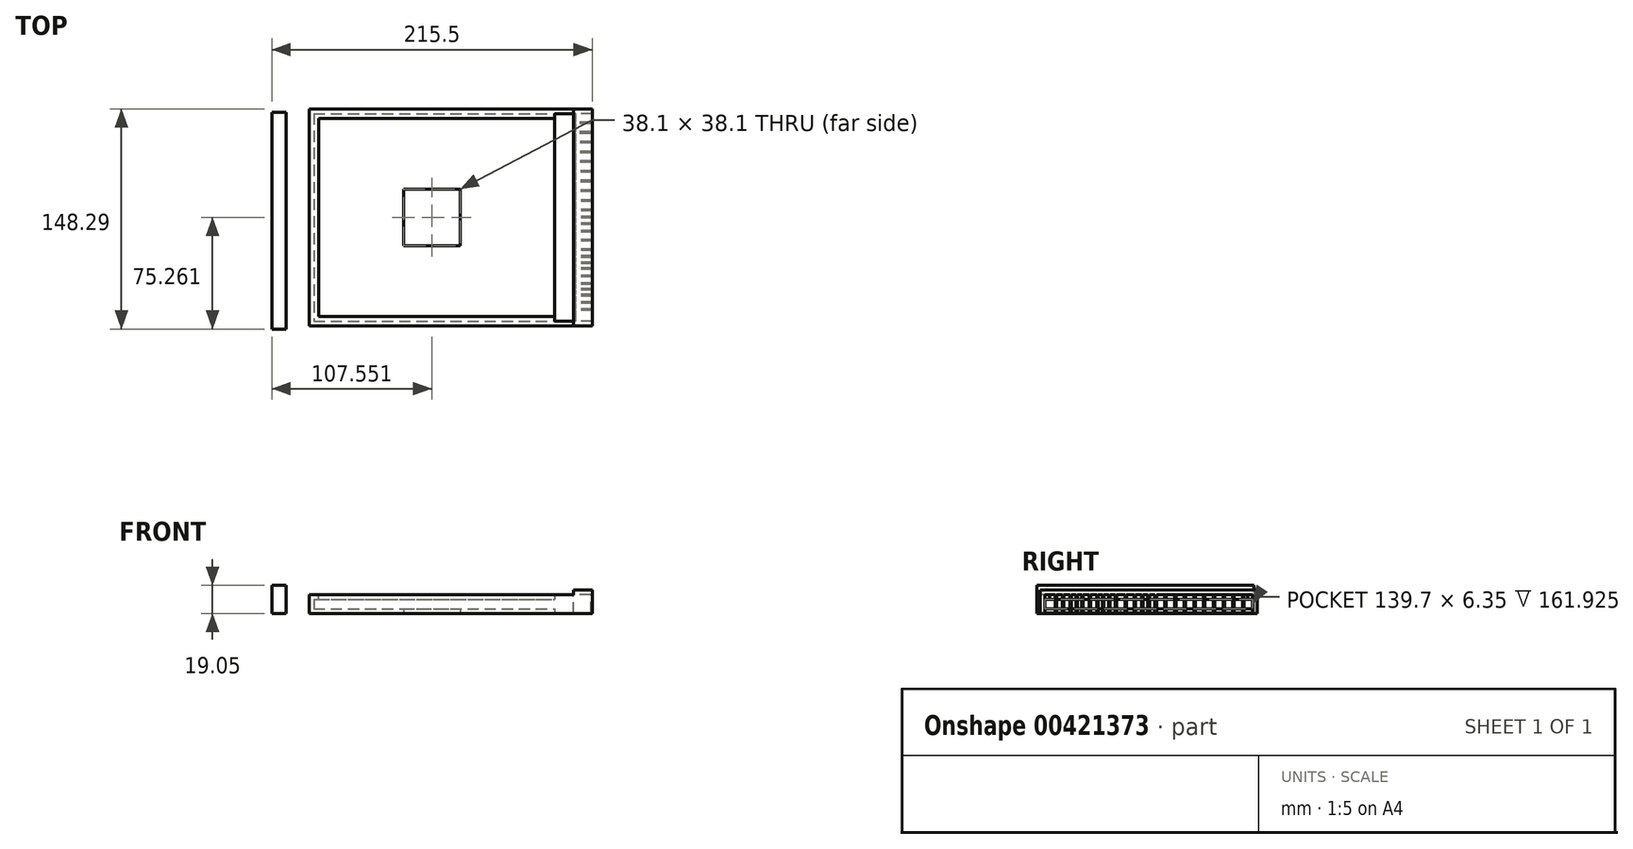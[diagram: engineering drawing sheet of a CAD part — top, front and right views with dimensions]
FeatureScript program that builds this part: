
annotation { "Feature Type Name" : "Feature", "Feature Type Description" : "" }
export const myFeature = defineFeature(function(context is Context, id is Id, definition is map)
    precondition{}
    {
        {
            var Q0;
            Q0=qCreatedBy(makeId("Top.planeOp"),FACE);
            var sketch = newSketch(context, id + "F0", { "sketchPlane" : qUnion([Q0])});
            skLineSegment(sketch, "E0.right", {"start": v(9.16, 77.9) * mm, "end": v(9.16, -42.76) * mm});
            skLineSegment(sketch, "E1.bottom", {"start": v(-155.94, 100.12) * mm, "end": v(9.16, 100.12) * mm});
            skLineSegment(sketch, "E1.top", {"start": v(-155.94, -45.93) * mm, "end": v(9.16, -45.93) * mm});
            skLineSegment(sketch, "E1.left", {"start": v(-155.94, 100.12) * mm, "end": v(-155.94, -45.93) * mm});
            skLineSegment(sketch, "E2", {"start": v(9.16, -42.76) * mm, "end": v(9.16, -45.93) * mm});
            skLineSegment(sketch, "E3", {"start": v(9.16, 77.9) * mm, "end": v(9.16, 100.12) * mm});
            skLineSegment(sketch, "E4.bottom", {"start": v(-92.44, 8.04) * mm, "end": v(-54.34, 8.04) * mm});
            skLineSegment(sketch, "E4.top", {"start": v(-92.44, 46.14) * mm, "end": v(-54.34, 46.14) * mm});
            skLineSegment(sketch, "E4.left", {"start": v(-92.44, 8.04) * mm, "end": v(-92.44, 46.14) * mm});
            skLineSegment(sketch, "E4.right", {"start": v(-54.34, 8.04) * mm, "end": v(-54.34, 46.14) * mm});
            skSolve(sketch);
        }
        {
            var Q0;
            Q0=makeQuery(id+"F0.imprint","IMPRINT",FACE,{"disambiguationData":[TD([[makeQuery(id+"F0.imprint","IMPRINT",EDGE,{"derivedFrom":sQuery(id+"F0.wireOp",EDGE,"E0.right")}),-1.0]])]});
            extrude(context, id + "F1", {"entities" : qUnion([Q0]), "depth" : 12.7 * mm});
        }
        {
            var Q0;
            Q0=makeQuery(id+"F1.opExtrude","SWEPT_FACE",FACE,{"disambiguationData":[OSD([sQuery(id+"F0.wireOp",EDGE,"E0.right"),sQuery(id+"F0.wireOp",EDGE,"E2"),sQuery(id+"F0.wireOp",EDGE,"E3")])]});
            var sketch = newSketch(context, id + "F2", { "sketchPlane" : qUnion([Q0])});
            skLineSegment(sketch, "E5.bottom", {"start": v(96.94, 9.52) * mm, "end": v(-42.76, 9.52) * mm});
            skLineSegment(sketch, "E5.top", {"start": v(96.94, 3.17) * mm, "end": v(-42.76, 3.17) * mm});
            skLineSegment(sketch, "E5.left", {"start": v(96.94, 9.52) * mm, "end": v(96.94, 3.17) * mm});
            skLineSegment(sketch, "E5.right", {"start": v(-42.76, 9.52) * mm, "end": v(-42.76, 3.17) * mm});
            skSolve(sketch);
        }
        {
            var Q0;
            Q0 = qSketchRegion(id + "F2", true);
            extrude(context, id + "F3", {"entities" : qUnion([Q0]), "operationType" : NewBodyOperationType.REMOVE, "oppositeDirection" : true, "depth" : 161.92 * mm});
        }
        {
            var Q0;
            Q0=makeQuery(id+"F1.opExtrude","CAP_FACE",FACE,{"disambiguationData":[OSD([sQuery(id+"F0.wireOp",EDGE,"E0.right"),sQuery(id+"F0.wireOp",EDGE,"E1.bottom"),sQuery(id+"F0.wireOp",EDGE,"E1.top"),sQuery(id+"F0.wireOp",EDGE,"E1.left"),sQuery(id+"F0.wireOp",EDGE,"E2"),sQuery(id+"F0.wireOp",EDGE,"E3")])],"isStart":false});
            var sketch = newSketch(context, id + "F4", { "sketchPlane" : qUnion([Q0])});
            skLineSegment(sketch, "E6.bottom", {"start": v(-149.59, 93.77) * mm, "end": v(9.16, 93.77) * mm});
            skLineSegment(sketch, "E6.top", {"start": v(-149.59, -39.58) * mm, "end": v(9.16, -39.58) * mm});
            skLineSegment(sketch, "E6.left", {"start": v(-149.59, 93.77) * mm, "end": v(-149.59, -39.58) * mm});
            skLineSegment(sketch, "E6.right", {"start": v(9.16, 93.77) * mm, "end": v(9.16, -39.58) * mm});
            skPoint(sketch, "E7.end.orphan", {"position": v(-149.59, 30.07) * mm});
            skPoint(sketch, "E7.start.orphan", {"position": v(-155.94, 30.07) * mm});
            skSolve(sketch);
        }
        {
            var Q0;
            Q0=makeQuery(id+"F4.imprint","IMPRINT",FACE,{"disambiguationData":[TD([[makeQuery(id+"F4.imprint","IMPRINT",EDGE,{"derivedFrom":sQuery(id+"F4.wireOp",EDGE,"E6.bottom")}),-1.0]])]});
            extrude(context, id + "F5", {"entities" : qUnion([Q0]), "operationType" : NewBodyOperationType.REMOVE, "oppositeDirection" : true, "depth" : 3.17 * mm});
        }
        {
            var Q0;
            Q0=makeQuery(id+"F1.opExtrude","SWEPT_FACE",FACE,{"disambiguationData":[OSD([sQuery(id+"F0.wireOp",EDGE,"E0.right"),sQuery(id+"F0.wireOp",EDGE,"E2"),sQuery(id+"F0.wireOp",EDGE,"E3")])]});
            var sketch = newSketch(context, id + "F6", { "sketchPlane" : qUnion([Q0])});
            skLineSegment(sketch, "E8", {"start": v(-42.76, 12.7) * mm, "end": v(-42.76, 0) * mm});
            skLineSegment(sketch, "E9", {"start": v(96.94, 12.7) * mm, "end": v(96.94, 0) * mm});
            skSolve(sketch);
        }
        {
            var Q0;
            {var subQ0=sQuery(id+"F0.wireOp",EDGE,"E2");var subQ1=sQuery(id+"F0.wireOp",EDGE,"E1.top");var subQ2=makeQuery(id+"F1.opExtrude","SWEPT_EDGE",EDGE,{"disambiguationData":[OSD([subQ1,subQ0])]});Q0=makeQuery(id+"F6.imprint","IMPRINT",FACE,{"disambiguationData":[TD([[makeQuery(id+"F6.imprint","IMPRINT",EDGE,{"derivedFrom":subQ2}),1.0]])]});}
            var Q1;
            {var subQ0=sQuery(id+"F0.wireOp",EDGE,"E3");var subQ1=sQuery(id+"F0.wireOp",EDGE,"E1.bottom");var subQ2=makeQuery(id+"F1.opExtrude","SWEPT_EDGE",EDGE,{"disambiguationData":[OSD([subQ1,subQ0])]});Q1=makeQuery(id+"F6.imprint","IMPRINT",FACE,{"disambiguationData":[TD([[makeQuery(id+"F6.imprint","IMPRINT",EDGE,{"derivedFrom":subQ2}),-1.0]])]});}
            extrude(context, id + "F7", {"entities" : qUnion([Q0, Q1]), "operationType" : NewBodyOperationType.ADD, "depth" : 25.4 * mm});
        }
        {
            var Q0;
            {var subQ0=sQuery(id+"F0.wireOp",EDGE,"E3");var subQ1=sQuery(id+"F0.wireOp",EDGE,"E2");var subQ2=sQuery(id+"F0.wireOp",EDGE,"E0.right");var subQ3=makeQuery(id+"F1.opExtrude","CAP_EDGE",EDGE,{"disambiguationData":[OSD([subQ2,subQ1,subQ0])],"isStart":true});var subQ4=sQuery(id+"F0.wireOp",EDGE,"E1.top");var subQ5=sQuery(id+"F0.wireOp",EDGE,"E1.bottom");Q0=makeQuery(id+"F7.boolean.opBoolean","MERGE",FACE,{"derivedFrom":[makeQuery(id+"F1.opExtrude","CAP_FACE",FACE,{"disambiguationData":[OSD([subQ2,subQ5,subQ4,sQuery(id+"F0.wireOp",EDGE,"E1.left"),subQ1,subQ0])],"isStart":true}),makeQuery(id+"F7.opExtrude","SWEPT_FACE",FACE,{"disambiguationData":[OSD([subQ2,subQ1,subQ0]),TDD([makeQuery(id+"F6.imprint","IMPRINT",EDGE,{"disambiguationData":[TD([[makeQuery(id+"F6.imprint","INTERSECT",VERTEX,{"derivedFrom":[subQ3,sQuery(id+"F6.wireOp",EDGE,"E9")]}),1.0]])],"derivedFrom":subQ3})])]}),makeQuery(id+"F7.opExtrude","SWEPT_FACE",FACE,{"disambiguationData":[OSD([subQ2,subQ1,subQ0]),TDD([makeQuery(id+"F6.imprint","IMPRINT",EDGE,{"disambiguationData":[TD([[makeQuery(id+"F6.imprint","INTERSECT",VERTEX,{"derivedFrom":[subQ3,sQuery(id+"F6.wireOp",EDGE,"E8")]}),-1.0]])],"derivedFrom":subQ3})])]})]});}
            var sketch = newSketch(context, id + "F8", { "sketchPlane" : qUnion([Q0])});
            skPoint(sketch, "E10.0", {"position": v(-180.94, 48.17) * mm});
            skLineSegment(sketch, "E11.0", {"start": v(-155.94, -100.12) * mm, "end": v(34.56, -100.12) * mm});
            skLineSegment(sketch, "E12.bottom", {"start": v(-180.94, 48.17) * mm, "end": v(-171.41, 48.17) * mm});
            skLineSegment(sketch, "E12.left", {"start": v(-180.94, 48.17) * mm, "end": v(-180.94, -97.88) * mm});
            skLineSegment(sketch, "E12.right", {"start": v(-171.41, 48.17) * mm, "end": v(-171.41, -97.88) * mm});
            skLineSegment(sketch, "E13", {"start": v(-171.41, -97.88) * mm, "end": v(-180.94, -97.88) * mm});
            skSolve(sketch);
        }
        {
            var Q0;
            Q0=makeQuery(id+"F8.imprint","IMPRINT",FACE,{"disambiguationData":[TD([[makeQuery(id+"F8.imprint","IMPRINT",EDGE,{"derivedFrom":sQuery(id+"F8.wireOp",EDGE,"E12.bottom")}),-1.0]])]});
            extrude(context, id + "F9", {"entities" : qUnion([Q0]), "oppositeDirection" : true, "depth" : 19.05 * mm});
        }
        {
            var Q0;
            {var subQ0=sQuery(id+"F0.wireOp",EDGE,"E1.top");Q0=makeQuery(id+"F9.boolean.opBoolean","MERGE",FACE,{"derivedFrom":[makeQuery(id+"F7.boolean.opBoolean","MERGE",FACE,{"derivedFrom":[makeQuery(id+"F1.opExtrude","SWEPT_FACE",FACE,{"disambiguationData":[OSD([subQ0])]}),makeQuery(id+"F7.opExtrude","SWEPT_FACE",FACE,{"disambiguationData":[OSD([subQ0,sQuery(id+"F0.wireOp",EDGE,"E2")])]})]}),makeQuery(id+"F9.opExtrude","SWEPT_FACE",FACE,{"disambiguationData":[OSD([sQuery(id+"F8.wireOp",EDGE,"E12.bottom")])]})]});}
            var sketch = newSketch(context, id + "F10", { "sketchPlane" : qUnion([Q0])});
            skLineSegment(sketch, "E14.bottom", {"start": v(34.56, 12.7) * mm, "end": v(21.86, 12.7) * mm});
            skLineSegment(sketch, "E14.top", {"start": v(34.56, 15.88) * mm, "end": v(21.86, 15.88) * mm});
            skLineSegment(sketch, "E14.left", {"start": v(34.56, 12.7) * mm, "end": v(34.56, 15.88) * mm});
            skLineSegment(sketch, "E14.right", {"start": v(21.86, 12.7) * mm, "end": v(21.86, 15.88) * mm});
            skSolve(sketch);
        }
        {
            var Q0;
            Q0=makeQuery(id+"F10.imprint","IMPRINT",FACE,{"disambiguationData":[TD([[makeQuery(id+"F10.imprint","IMPRINT",EDGE,{"derivedFrom":sQuery(id+"F10.wireOp",EDGE,"E14.bottom")}),1.0]])]});
            extrude(context, id + "F11", {"entities" : qUnion([Q0]), "operationType" : NewBodyOperationType.ADD, "oppositeDirection" : true, "depth" : 146.05 * mm});
        }
        {
            var Q0;
            Q0=makeQuery(id+"F11.opExtrude","SWEPT_FACE",FACE,{"disambiguationData":[OSD([sQuery(id+"F10.wireOp",EDGE,"E14.bottom")])]});
            var sketch = newSketch(context, id + "F12", { "sketchPlane" : qUnion([Q0])});
            skLineSegment(sketch, "E15.bottom", {"start": v(34.56, 35.67) * mm, "end": v(21.86, 35.67) * mm});
            skLineSegment(sketch, "E15.top", {"start": v(34.56, 34.67) * mm, "end": v(21.86, 34.67) * mm});
            skLineSegment(sketch, "E15.left", {"start": v(34.56, 35.67) * mm, "end": v(34.56, 34.67) * mm});
            skLineSegment(sketch, "E15.right", {"start": v(21.86, 35.67) * mm, "end": v(21.86, 34.67) * mm});
            skLineSegment(sketch, "E16.bottom", {"start": v(34.56, 25.88) * mm, "end": v(21.86, 25.88) * mm});
            skLineSegment(sketch, "E16.top", {"start": v(34.56, 24.88) * mm, "end": v(21.86, 24.88) * mm});
            skLineSegment(sketch, "E16.left", {"start": v(34.56, 25.88) * mm, "end": v(34.56, 24.88) * mm});
            skLineSegment(sketch, "E16.right", {"start": v(21.86, 25.88) * mm, "end": v(21.86, 24.88) * mm});
            skLineSegment(sketch, "E17.bottom", {"start": v(34.56, 21.93) * mm, "end": v(21.86, 21.93) * mm});
            skLineSegment(sketch, "E17.top", {"start": v(34.56, 20.93) * mm, "end": v(21.86, 20.93) * mm});
            skLineSegment(sketch, "E17.left", {"start": v(34.56, 21.93) * mm, "end": v(34.56, 20.93) * mm});
            skLineSegment(sketch, "E17.right", {"start": v(21.86, 21.93) * mm, "end": v(21.86, 20.93) * mm});
            skLineSegment(sketch, "E18.bottom", {"start": v(34.56, 18) * mm, "end": v(21.86, 18) * mm});
            skLineSegment(sketch, "E18.top", {"start": v(34.56, 17) * mm, "end": v(21.86, 17) * mm});
            skLineSegment(sketch, "E18.left", {"start": v(34.56, 18) * mm, "end": v(34.56, 17) * mm});
            skLineSegment(sketch, "E18.right", {"start": v(21.86, 18) * mm, "end": v(21.86, 17) * mm});
            skLineSegment(sketch, "E19.bottom", {"start": v(34.56, 30.9) * mm, "end": v(21.86, 30.9) * mm});
            skLineSegment(sketch, "E19.top", {"start": v(34.56, 29.9) * mm, "end": v(21.86, 29.9) * mm});
            skLineSegment(sketch, "E19.left", {"start": v(34.56, 30.9) * mm, "end": v(34.56, 29.9) * mm});
            skLineSegment(sketch, "E19.right", {"start": v(21.86, 30.9) * mm, "end": v(21.86, 29.9) * mm});
            skLineSegment(sketch, "E20.bottom", {"start": v(34.56, 12.93) * mm, "end": v(21.86, 12.93) * mm});
            skLineSegment(sketch, "E20.top", {"start": v(34.56, 11.93) * mm, "end": v(21.86, 11.93) * mm});
            skLineSegment(sketch, "E20.left", {"start": v(34.56, 12.93) * mm, "end": v(34.56, 11.93) * mm});
            skLineSegment(sketch, "E20.right", {"start": v(21.86, 12.93) * mm, "end": v(21.86, 11.93) * mm});
            skLineSegment(sketch, "E21.bottom", {"start": v(34.56, 7.84) * mm, "end": v(21.86, 7.84) * mm});
            skLineSegment(sketch, "E21.top", {"start": v(34.56, 6.84) * mm, "end": v(21.86, 6.84) * mm});
            skLineSegment(sketch, "E21.left", {"start": v(34.56, 7.84) * mm, "end": v(34.56, 6.84) * mm});
            skLineSegment(sketch, "E21.right", {"start": v(21.86, 7.84) * mm, "end": v(21.86, 6.84) * mm});
            skLineSegment(sketch, "E22.bottom", {"start": v(34.56, 4) * mm, "end": v(21.86, 4) * mm});
            skLineSegment(sketch, "E22.top", {"start": v(34.56, 3) * mm, "end": v(21.86, 3) * mm});
            skLineSegment(sketch, "E22.left", {"start": v(34.56, 4) * mm, "end": v(34.56, 3) * mm});
            skLineSegment(sketch, "E22.right", {"start": v(21.86, 4) * mm, "end": v(21.86, 3) * mm});
            skLineSegment(sketch, "E23.bottom", {"start": v(34.56, -0.16) * mm, "end": v(21.86, -0.16) * mm});
            skLineSegment(sketch, "E23.top", {"start": v(34.56, -1.16) * mm, "end": v(21.86, -1.16) * mm});
            skLineSegment(sketch, "E23.left", {"start": v(34.56, -0.16) * mm, "end": v(34.56, -1.16) * mm});
            skLineSegment(sketch, "E23.right", {"start": v(21.86, -0.16) * mm, "end": v(21.86, -1.16) * mm});
            skLineSegment(sketch, "E24.bottom", {"start": v(34.56, -4.65) * mm, "end": v(21.86, -4.65) * mm});
            skLineSegment(sketch, "E24.top", {"start": v(34.56, -5.65) * mm, "end": v(21.86, -5.65) * mm});
            skLineSegment(sketch, "E24.left", {"start": v(34.56, -4.65) * mm, "end": v(34.56, -5.65) * mm});
            skLineSegment(sketch, "E24.right", {"start": v(21.86, -4.65) * mm, "end": v(21.86, -5.65) * mm});
            skLineSegment(sketch, "E25.bottom", {"start": v(34.56, -11.24) * mm, "end": v(21.86, -11.24) * mm});
            skLineSegment(sketch, "E25.top", {"start": v(34.56, -12.24) * mm, "end": v(21.86, -12.24) * mm});
            skLineSegment(sketch, "E25.left", {"start": v(34.56, -11.24) * mm, "end": v(34.56, -12.24) * mm});
            skLineSegment(sketch, "E25.right", {"start": v(21.86, -11.24) * mm, "end": v(21.86, -12.24) * mm});
            skLineSegment(sketch, "E26.bottom", {"start": v(34.56, -17.2) * mm, "end": v(21.86, -17.2) * mm});
            skLineSegment(sketch, "E26.top", {"start": v(34.56, -18.2) * mm, "end": v(21.86, -18.2) * mm});
            skLineSegment(sketch, "E26.left", {"start": v(34.56, -17.2) * mm, "end": v(34.56, -18.2) * mm});
            skLineSegment(sketch, "E26.right", {"start": v(21.86, -17.2) * mm, "end": v(21.86, -18.2) * mm});
            skLineSegment(sketch, "E27.bottom", {"start": v(34.56, -22.35) * mm, "end": v(21.86, -22.35) * mm});
            skLineSegment(sketch, "E27.top", {"start": v(34.56, -23.35) * mm, "end": v(21.86, -23.35) * mm});
            skLineSegment(sketch, "E27.left", {"start": v(34.56, -22.35) * mm, "end": v(34.56, -23.35) * mm});
            skLineSegment(sketch, "E27.right", {"start": v(21.86, -22.35) * mm, "end": v(21.86, -23.35) * mm});
            skLineSegment(sketch, "E28.bottom", {"start": v(34.6, -26.6) * mm, "end": v(21.9, -26.6) * mm});
            skLineSegment(sketch, "E28.top", {"start": v(34.6, -27.6) * mm, "end": v(21.9, -27.6) * mm});
            skLineSegment(sketch, "E28.left", {"start": v(34.6, -26.6) * mm, "end": v(34.6, -27.6) * mm});
            skLineSegment(sketch, "E28.right", {"start": v(21.9, -26.6) * mm, "end": v(21.9, -27.6) * mm});
            skLineSegment(sketch, "E29.bottom", {"start": v(34.6, -31.37) * mm, "end": v(21.9, -31.37) * mm});
            skLineSegment(sketch, "E29.top", {"start": v(34.6, -32.37) * mm, "end": v(21.9, -32.37) * mm});
            skLineSegment(sketch, "E29.left", {"start": v(34.6, -31.37) * mm, "end": v(34.6, -32.37) * mm});
            skLineSegment(sketch, "E29.right", {"start": v(21.9, -31.37) * mm, "end": v(21.9, -32.37) * mm});
            skLineSegment(sketch, "E30.0.1.0", {"start": v(34.5, -37.9) * mm, "end": v(21.8, -37.9) * mm});
            skLineSegment(sketch, "E30.0.1.1", {"start": v(34.5, -38.9) * mm, "end": v(21.8, -38.9) * mm});
            skLineSegment(sketch, "E30.0.1.2", {"start": v(21.8, -37.9) * mm, "end": v(21.8, -38.9) * mm});
            skLineSegment(sketch, "E30.0.1.3", {"start": v(34.5, -37.9) * mm, "end": v(34.5, -38.9) * mm});
            skLineSegment(sketch, "E30.0.2.0", {"start": v(34.4, -44.43) * mm, "end": v(21.7, -44.43) * mm});
            skLineSegment(sketch, "E30.0.2.1", {"start": v(34.4, -45.43) * mm, "end": v(21.7, -45.43) * mm});
            skLineSegment(sketch, "E30.0.2.2", {"start": v(21.7, -44.43) * mm, "end": v(21.7, -45.43) * mm});
            skLineSegment(sketch, "E30.0.2.3", {"start": v(34.4, -44.43) * mm, "end": v(34.4, -45.43) * mm});
            skLineSegment(sketch, "E30.0.3.0", {"start": v(34.28, -50.97) * mm, "end": v(21.58, -50.97) * mm});
            skLineSegment(sketch, "E30.0.3.1", {"start": v(34.28, -51.97) * mm, "end": v(21.58, -51.97) * mm});
            skLineSegment(sketch, "E30.0.3.2", {"start": v(21.58, -50.97) * mm, "end": v(21.58, -51.97) * mm});
            skLineSegment(sketch, "E30.0.3.3", {"start": v(34.28, -50.97) * mm, "end": v(34.28, -51.97) * mm});
            skLineSegment(sketch, "E30.0.4.0", {"start": v(34.18, -57.5) * mm, "end": v(21.48, -57.5) * mm});
            skLineSegment(sketch, "E30.0.4.1", {"start": v(34.18, -58.5) * mm, "end": v(21.48, -58.5) * mm});
            skLineSegment(sketch, "E30.0.4.2", {"start": v(21.48, -57.5) * mm, "end": v(21.48, -58.5) * mm});
            skLineSegment(sketch, "E30.0.4.3", {"start": v(34.18, -57.5) * mm, "end": v(34.18, -58.5) * mm});
            skLineSegment(sketch, "E30.0.5.0", {"start": v(34.07, -64.04) * mm, "end": v(21.37, -64.04) * mm});
            skLineSegment(sketch, "E30.0.5.1", {"start": v(34.07, -65.04) * mm, "end": v(21.37, -65.04) * mm});
            skLineSegment(sketch, "E30.0.5.2", {"start": v(21.37, -64.04) * mm, "end": v(21.37, -65.04) * mm});
            skLineSegment(sketch, "E30.0.5.3", {"start": v(34.07, -64.04) * mm, "end": v(34.07, -65.04) * mm});
            skLineSegment(sketch, "E30.0.6.0", {"start": v(33.96, -70.57) * mm, "end": v(21.26, -70.57) * mm});
            skLineSegment(sketch, "E30.0.6.1", {"start": v(33.96, -71.57) * mm, "end": v(21.26, -71.57) * mm});
            skLineSegment(sketch, "E30.0.6.2", {"start": v(21.26, -70.57) * mm, "end": v(21.26, -71.57) * mm});
            skLineSegment(sketch, "E30.0.6.3", {"start": v(33.96, -70.57) * mm, "end": v(33.96, -71.57) * mm});
            skLineSegment(sketch, "E30.0.7.0", {"start": v(33.85, -77.1) * mm, "end": v(21.15, -77.1) * mm});
            skLineSegment(sketch, "E30.0.7.1", {"start": v(33.85, -78.1) * mm, "end": v(21.15, -78.1) * mm});
            skLineSegment(sketch, "E30.0.7.2", {"start": v(21.15, -77.1) * mm, "end": v(21.15, -78.1) * mm});
            skLineSegment(sketch, "E30.0.7.3", {"start": v(33.85, -77.1) * mm, "end": v(33.85, -78.1) * mm});
            skLineSegment(sketch, "E30.0.8.0", {"start": v(33.75, -83.64) * mm, "end": v(21.05, -83.64) * mm});
            skLineSegment(sketch, "E30.0.8.1", {"start": v(33.75, -84.64) * mm, "end": v(21.05, -84.64) * mm});
            skLineSegment(sketch, "E30.0.8.2", {"start": v(21.05, -83.64) * mm, "end": v(21.05, -84.64) * mm});
            skLineSegment(sketch, "E30.0.8.3", {"start": v(33.75, -83.64) * mm, "end": v(33.75, -84.64) * mm});
            skLineSegment(sketch, "E30.0.9.0", {"start": v(33.64, -90.17) * mm, "end": v(20.94, -90.17) * mm});
            skLineSegment(sketch, "E30.0.9.1", {"start": v(33.64, -91.17) * mm, "end": v(20.94, -91.17) * mm});
            skLineSegment(sketch, "E30.0.9.2", {"start": v(20.94, -90.17) * mm, "end": v(20.94, -91.17) * mm});
            skLineSegment(sketch, "E30.0.9.3", {"start": v(33.64, -90.17) * mm, "end": v(33.64, -91.17) * mm});
            skLineSegment(sketch, "E30.direction1", {"start": v(21.9, -32.37) * mm, "end": v(46.9, -32.37) * mm, "construction": true});
            skLineSegment(sketch, "E30.direction2", {"start": v(21.9, -32.37) * mm, "end": v(21.8, -38.9) * mm, "construction": true});
            skSolve(sketch);
        }
        {
            var Q0;
            Q0=makeQuery(id+"F12.imprint","IMPRINT",FACE,{"disambiguationData":[TD([[makeQuery(id+"F12.imprint","IMPRINT",EDGE,{"derivedFrom":sQuery(id+"F12.wireOp",EDGE,"E15.bottom")}),1.0]])]});
            var Q1;
            Q1=makeQuery(id+"F12.imprint","IMPRINT",FACE,{"disambiguationData":[TD([[makeQuery(id+"F12.imprint","IMPRINT",EDGE,{"derivedFrom":sQuery(id+"F12.wireOp",EDGE,"E19.bottom")}),1.0]])]});
            var Q2;
            Q2=makeQuery(id+"F12.imprint","IMPRINT",FACE,{"disambiguationData":[TD([[makeQuery(id+"F12.imprint","IMPRINT",EDGE,{"derivedFrom":sQuery(id+"F12.wireOp",EDGE,"E16.bottom")}),1.0]])]});
            var Q3;
            Q3=makeQuery(id+"F12.imprint","IMPRINT",FACE,{"disambiguationData":[TD([[makeQuery(id+"F12.imprint","IMPRINT",EDGE,{"derivedFrom":sQuery(id+"F12.wireOp",EDGE,"E17.bottom")}),1.0]])]});
            var Q4;
            Q4=makeQuery(id+"F12.imprint","IMPRINT",FACE,{"disambiguationData":[TD([[makeQuery(id+"F12.imprint","IMPRINT",EDGE,{"derivedFrom":sQuery(id+"F12.wireOp",EDGE,"E18.bottom")}),1.0]])]});
            var Q5;
            Q5=makeQuery(id+"F12.imprint","IMPRINT",FACE,{"disambiguationData":[TD([[makeQuery(id+"F12.imprint","IMPRINT",EDGE,{"derivedFrom":sQuery(id+"F12.wireOp",EDGE,"E20.bottom")}),1.0]])]});
            var Q6;
            Q6=makeQuery(id+"F12.imprint","IMPRINT",FACE,{"disambiguationData":[TD([[makeQuery(id+"F12.imprint","IMPRINT",EDGE,{"derivedFrom":sQuery(id+"F12.wireOp",EDGE,"E21.bottom")}),1.0]])]});
            var Q7;
            Q7=makeQuery(id+"F12.imprint","IMPRINT",FACE,{"disambiguationData":[TD([[makeQuery(id+"F12.imprint","IMPRINT",EDGE,{"derivedFrom":sQuery(id+"F12.wireOp",EDGE,"E22.bottom")}),1.0]])]});
            var Q8;
            Q8=makeQuery(id+"F12.imprint","IMPRINT",FACE,{"disambiguationData":[TD([[makeQuery(id+"F12.imprint","IMPRINT",EDGE,{"derivedFrom":sQuery(id+"F12.wireOp",EDGE,"E23.bottom")}),1.0]])]});
            var Q9;
            Q9=makeQuery(id+"F12.imprint","IMPRINT",FACE,{"disambiguationData":[TD([[makeQuery(id+"F12.imprint","IMPRINT",EDGE,{"derivedFrom":sQuery(id+"F12.wireOp",EDGE,"E24.bottom")}),1.0]])]});
            var Q10;
            Q10=makeQuery(id+"F12.imprint","IMPRINT",FACE,{"disambiguationData":[TD([[makeQuery(id+"F12.imprint","IMPRINT",EDGE,{"derivedFrom":sQuery(id+"F12.wireOp",EDGE,"E25.bottom")}),1.0]])]});
            var Q11;
            Q11=makeQuery(id+"F12.imprint","IMPRINT",FACE,{"disambiguationData":[TD([[makeQuery(id+"F12.imprint","IMPRINT",EDGE,{"derivedFrom":sQuery(id+"F12.wireOp",EDGE,"E26.bottom")}),1.0]])]});
            var Q12;
            Q12=makeQuery(id+"F12.imprint","IMPRINT",FACE,{"disambiguationData":[TD([[makeQuery(id+"F12.imprint","IMPRINT",EDGE,{"derivedFrom":sQuery(id+"F12.wireOp",EDGE,"E27.bottom")}),1.0]])]});
            var Q13;
            {var subQ0=sQuery(id+"F12.wireOp",EDGE,"E28.right");Q13=makeQuery(id+"F12.imprint","IMPRINT",FACE,{"disambiguationData":[TD([[makeQuery(id+"F12.imprint","IMPRINT",EDGE,{"derivedFrom":subQ0}),1.0]])]});}
            var Q14;
            {var subQ0=sQuery(id+"F12.wireOp",EDGE,"E29.right");Q14=makeQuery(id+"F12.imprint","IMPRINT",FACE,{"disambiguationData":[TD([[makeQuery(id+"F12.imprint","IMPRINT",EDGE,{"derivedFrom":subQ0}),1.0]])]});}
            var Q15;
            {var subQ0=sQuery(id+"F12.wireOp",EDGE,"1c767b76-1ce6-4311-9e5b-dfddebc06e8c.right");Q15=makeQuery(id+"F12.imprint","IMPRINT",FACE,{"disambiguationData":[TD([[makeQuery(id+"F12.imprint","IMPRINT",EDGE,{"derivedFrom":subQ0}),1.0]])]});}
            var Q16;
            {var subQ0=sQuery(id+"F12.wireOp",EDGE,"bfbf2cdf-8170-4018-8a6d-dc8bf7d19348.right");Q16=makeQuery(id+"F12.imprint","IMPRINT",FACE,{"disambiguationData":[TD([[makeQuery(id+"F12.imprint","IMPRINT",EDGE,{"derivedFrom":subQ0}),1.0]])]});}
            var Q17;
            {var subQ0=sQuery(id+"F12.wireOp",EDGE,"00d62c1f-5c08-4788-912a-3ac5d758a5cb.right");Q17=makeQuery(id+"F12.imprint","IMPRINT",FACE,{"disambiguationData":[TD([[makeQuery(id+"F12.imprint","IMPRINT",EDGE,{"derivedFrom":subQ0}),1.0]])]});}
            var Q18;
            {var subQ0=sQuery(id+"F12.wireOp",EDGE,"0aae401a-74db-45b8-a4a4-0d89c3569b9f.right");Q18=makeQuery(id+"F12.imprint","IMPRINT",FACE,{"disambiguationData":[TD([[makeQuery(id+"F12.imprint","IMPRINT",EDGE,{"derivedFrom":subQ0}),1.0]])]});}
            var Q19;
            {var subQ0=sQuery(id+"F12.wireOp",EDGE,"fec7dae8-34f9-4537-b75b-9f8a8f20716f.right");Q19=makeQuery(id+"F12.imprint","IMPRINT",FACE,{"disambiguationData":[TD([[makeQuery(id+"F12.imprint","IMPRINT",EDGE,{"derivedFrom":subQ0}),1.0]])]});}
            var Q20;
            {var subQ0=sQuery(id+"F12.wireOp",EDGE,"43953527-2e33-448e-8b7c-f1fa6cddecf0.right");Q20=makeQuery(id+"F12.imprint","IMPRINT",FACE,{"disambiguationData":[TD([[makeQuery(id+"F12.imprint","IMPRINT",EDGE,{"derivedFrom":subQ0}),1.0]])]});}
            var Q21;
            {var subQ0=sQuery(id+"F12.wireOp",EDGE,"a510151a-f6a3-42e3-bfe8-577be6524428.right");Q21=makeQuery(id+"F12.imprint","IMPRINT",FACE,{"disambiguationData":[TD([[makeQuery(id+"F12.imprint","IMPRINT",EDGE,{"derivedFrom":subQ0}),1.0]])]});}
            var Q22;
            {var subQ0=sQuery(id+"F12.wireOp",EDGE,"1020d4eb-1593-4d40-b34b-e0bc60ceed5e.right");Q22=makeQuery(id+"F12.imprint","IMPRINT",FACE,{"disambiguationData":[TD([[makeQuery(id+"F12.imprint","IMPRINT",EDGE,{"derivedFrom":subQ0}),1.0]])]});}
            var Q23;
            {var subQ0=sQuery(id+"F12.wireOp",EDGE,"80ebdb32-ed2b-4c32-bbfd-e77552b5e031.bottom");Q23=makeQuery(id+"F12.imprint","IMPRINT",FACE,{"disambiguationData":[TD([[makeQuery(id+"F12.imprint","IMPRINT",EDGE,{"derivedFrom":subQ0}),1.0]])]});}
            var Q24;
            Q24=makeQuery(id+"F12.imprint","IMPRINT",FACE,{"disambiguationData":[TD([[makeQuery(id+"F12.imprint","IMPRINT",EDGE,{"derivedFrom":sQuery(id+"F12.wireOp",EDGE,"1c29ddfe-a8fd-45b3-a8c5-c6162b02b9a7.bottom")}),1.0]])]});
            var Q25;
            Q25=makeQuery(id+"F12.imprint","IMPRINT",FACE,{"disambiguationData":[TD([[makeQuery(id+"F12.imprint","IMPRINT",EDGE,{"derivedFrom":sQuery(id+"F12.wireOp",EDGE,"243fcd7a-51af-4c17-baf2-796151d44cde.bottom")}),1.0]])]});
            var Q26;
            {var subQ0=sQuery(id+"F12.wireOp",EDGE,"cd03d691-0da5-451e-81b7-96a068035b05.bottom");Q26=makeQuery(id+"F12.imprint","IMPRINT",FACE,{"disambiguationData":[TD([[makeQuery(id+"F12.imprint","IMPRINT",EDGE,{"derivedFrom":subQ0}),1.0]])]});}
            var Q27;
            {var subQ0=sQuery(id+"F12.wireOp",EDGE,"ecd5f52c-aac6-4163-a9f2-a9fe20fbabce.bottom");Q27=makeQuery(id+"F12.imprint","IMPRINT",FACE,{"disambiguationData":[TD([[makeQuery(id+"F12.imprint","IMPRINT",EDGE,{"derivedFrom":subQ0}),1.0]])]});}
            var Q28;
            {var subQ0=sQuery(id+"F12.wireOp",EDGE,"E30.0.2.3");Q28=makeQuery(id+"F12.imprint","IMPRINT",FACE,{"disambiguationData":[TD([[makeQuery(id+"F12.imprint","IMPRINT",EDGE,{"derivedFrom":subQ0}),-1.0]])]});}
            var Q29;
            {var subQ0=sQuery(id+"F12.wireOp",EDGE,"E30.0.3.3");Q29=makeQuery(id+"F12.imprint","IMPRINT",FACE,{"disambiguationData":[TD([[makeQuery(id+"F12.imprint","IMPRINT",EDGE,{"derivedFrom":subQ0}),-1.0]])]});}
            var Q30;
            {var subQ0=sQuery(id+"F12.wireOp",EDGE,"E30.0.1.3");Q30=makeQuery(id+"F12.imprint","IMPRINT",FACE,{"disambiguationData":[TD([[makeQuery(id+"F12.imprint","IMPRINT",EDGE,{"derivedFrom":subQ0}),-1.0]])]});}
            var Q31;
            {var subQ0=sQuery(id+"F12.wireOp",EDGE,"E30.0.9.3");Q31=makeQuery(id+"F12.imprint","IMPRINT",FACE,{"disambiguationData":[TD([[makeQuery(id+"F12.imprint","IMPRINT",EDGE,{"derivedFrom":subQ0}),-1.0]])]});}
            var Q32;
            {var subQ0=sQuery(id+"F12.wireOp",EDGE,"E30.0.8.3");Q32=makeQuery(id+"F12.imprint","IMPRINT",FACE,{"disambiguationData":[TD([[makeQuery(id+"F12.imprint","IMPRINT",EDGE,{"derivedFrom":subQ0}),-1.0]])]});}
            var Q33;
            {var subQ0=sQuery(id+"F12.wireOp",EDGE,"E30.0.7.3");Q33=makeQuery(id+"F12.imprint","IMPRINT",FACE,{"disambiguationData":[TD([[makeQuery(id+"F12.imprint","IMPRINT",EDGE,{"derivedFrom":subQ0}),-1.0]])]});}
            var Q34;
            {var subQ0=sQuery(id+"F12.wireOp",EDGE,"E30.0.6.3");Q34=makeQuery(id+"F12.imprint","IMPRINT",FACE,{"disambiguationData":[TD([[makeQuery(id+"F12.imprint","IMPRINT",EDGE,{"derivedFrom":subQ0}),-1.0]])]});}
            var Q35;
            {var subQ0=sQuery(id+"F12.wireOp",EDGE,"E30.0.5.3");Q35=makeQuery(id+"F12.imprint","IMPRINT",FACE,{"disambiguationData":[TD([[makeQuery(id+"F12.imprint","IMPRINT",EDGE,{"derivedFrom":subQ0}),-1.0]])]});}
            var Q36;
            {var subQ0=sQuery(id+"F12.wireOp",EDGE,"E30.0.4.3");Q36=makeQuery(id+"F12.imprint","IMPRINT",FACE,{"disambiguationData":[TD([[makeQuery(id+"F12.imprint","IMPRINT",EDGE,{"derivedFrom":subQ0}),-1.0]])]});}
            var Q37;
            {var subQ0=sQuery(id+"F0.wireOp",EDGE,"E3");var subQ1=sQuery(id+"F0.wireOp",EDGE,"E2");var subQ2=sQuery(id+"F0.wireOp",EDGE,"E0.right");var subQ3=makeQuery(id+"F1.opExtrude","CAP_EDGE",EDGE,{"disambiguationData":[OSD([subQ2,subQ1,subQ0])],"isStart":true});var subQ4=sQuery(id+"F0.wireOp",EDGE,"E1.top");var subQ5=sQuery(id+"F0.wireOp",EDGE,"E1.bottom");Q37=makeQuery(id+"F7.boolean.opBoolean","MERGE",FACE,{"derivedFrom":[makeQuery(id+"F1.opExtrude","CAP_FACE",FACE,{"disambiguationData":[OSD([subQ2,subQ5,subQ4,sQuery(id+"F0.wireOp",EDGE,"E1.left"),subQ1,subQ0])],"isStart":true}),makeQuery(id+"F7.opExtrude","SWEPT_FACE",FACE,{"disambiguationData":[OSD([subQ2,subQ1,subQ0]),TDD([makeQuery(id+"F6.imprint","IMPRINT",EDGE,{"disambiguationData":[TD([[makeQuery(id+"F6.imprint","INTERSECT",VERTEX,{"derivedFrom":[subQ3,sQuery(id+"F6.wireOp",EDGE,"E9")]}),1.0]])],"derivedFrom":subQ3})])]}),makeQuery(id+"F7.opExtrude","SWEPT_FACE",FACE,{"disambiguationData":[OSD([subQ2,subQ1,subQ0]),TDD([makeQuery(id+"F6.imprint","IMPRINT",EDGE,{"disambiguationData":[TD([[makeQuery(id+"F6.imprint","INTERSECT",VERTEX,{"derivedFrom":[subQ3,sQuery(id+"F6.wireOp",EDGE,"E8")]}),-1.0]])],"derivedFrom":subQ3})])]})]});}
            extrude(context, id + "F13", {"entities" : qUnion([Q0, Q1, Q2, Q3, Q4, Q5, Q6, Q7, Q8, Q9, Q10, Q11, Q12, Q13, Q14, Q15, Q16, Q17, Q18, Q19, Q20, Q21, Q22, Q23, Q24, Q25, Q26, Q27, Q28, Q29, Q30, Q31, Q32, Q33, Q34, Q35, Q36]), "operationType" : NewBodyOperationType.ADD, "endBound" : BoundingType.UP_TO_SURFACE, "endBoundEntityFace" : qUnion([Q37]), "depth" : 25 * mm});
        }
        {
            var Q0;
            {var subQ0=sQuery(id+"F0.wireOp",EDGE,"E3");var subQ1=sQuery(id+"F0.wireOp",EDGE,"E2");var subQ2=sQuery(id+"F0.wireOp",EDGE,"E0.right");var subQ3=makeQuery(id+"F1.opExtrude","CAP_EDGE",EDGE,{"disambiguationData":[OSD([subQ2,subQ1,subQ0])],"isStart":true});var subQ4=sQuery(id+"F0.wireOp",EDGE,"E1.top");var subQ5=sQuery(id+"F0.wireOp",EDGE,"E1.bottom");Q0=makeQuery(id+"F7.boolean.opBoolean","MERGE",FACE,{"derivedFrom":[makeQuery(id+"F1.opExtrude","CAP_FACE",FACE,{"disambiguationData":[OSD([subQ2,subQ5,subQ4,sQuery(id+"F0.wireOp",EDGE,"E1.left"),subQ1,subQ0])],"isStart":true}),makeQuery(id+"F7.opExtrude","SWEPT_FACE",FACE,{"disambiguationData":[OSD([subQ2,subQ1,subQ0]),TDD([makeQuery(id+"F6.imprint","IMPRINT",EDGE,{"disambiguationData":[TD([[makeQuery(id+"F6.imprint","INTERSECT",VERTEX,{"derivedFrom":[subQ3,sQuery(id+"F6.wireOp",EDGE,"E9")]}),1.0]])],"derivedFrom":subQ3})])]}),makeQuery(id+"F7.opExtrude","SWEPT_FACE",FACE,{"disambiguationData":[OSD([subQ2,subQ1,subQ0]),TDD([makeQuery(id+"F6.imprint","IMPRINT",EDGE,{"disambiguationData":[TD([[makeQuery(id+"F6.imprint","INTERSECT",VERTEX,{"derivedFrom":[subQ3,sQuery(id+"F6.wireOp",EDGE,"E8")]}),-1.0]])],"derivedFrom":subQ3})])]})]});}
            var sketch = newSketch(context, id + "F14", { "sketchPlane" : qUnion([Q0])});
            skLineSegment(sketch, "E31.bottom", {"start": v(23.45, 45.93) * mm, "end": v(34.56, 45.93) * mm});
            skLineSegment(sketch, "E31.top", {"start": v(23.45, -100.12) * mm, "end": v(34.56, -100.12) * mm});
            skLineSegment(sketch, "E31.left", {"start": v(23.45, 45.93) * mm, "end": v(23.45, -100.12) * mm});
            skLineSegment(sketch, "E31.right", {"start": v(34.56, 45.93) * mm, "end": v(34.56, -100.12) * mm});
            skSolve(sketch);
        }
        {
            var Q0;
            {var subQ0=sQuery(id+"F14.wireOp",EDGE,"E31.left");var subQ1=sQuery(id+"F6.wireOp",EDGE,"E8");var subQ2=sQuery(id+"F0.wireOp",EDGE,"E3");var subQ3=sQuery(id+"F0.wireOp",EDGE,"E2");var subQ4=sQuery(id+"F0.wireOp",EDGE,"E0.right");var subQ5=makeQuery(id+"F1.opExtrude","CAP_EDGE",EDGE,{"disambiguationData":[OSD([subQ4,subQ3,subQ2])],"isStart":true});var subQ6=makeQuery(id+"F7.opExtrude","SWEPT_EDGE",EDGE,{"disambiguationData":[OSD([subQ4,subQ3,subQ2,subQ1]),TDD([makeQuery(id+"F6.imprint","INTERSECT",VERTEX,{"derivedFrom":[subQ5,subQ1]})])]});var subQ7=makeQuery(id+"F14.imprint","INTERSECT",VERTEX,{"derivedFrom":[subQ6,subQ0]});Q0=makeQuery(id+"F14.imprint","IMPRINT",FACE,{"disambiguationData":[TD([[makeQuery(id+"F14.imprint","IMPRINT",EDGE,{"disambiguationData":[TD([[subQ7,-1.0]])],"derivedFrom":subQ0}),1.0]])]});}
            extrude(context, id + "F15", {"entities" : qUnion([Q0]), "operationType" : NewBodyOperationType.ADD, "oppositeDirection" : true, "depth" : .5 * mm});
        }
    });
